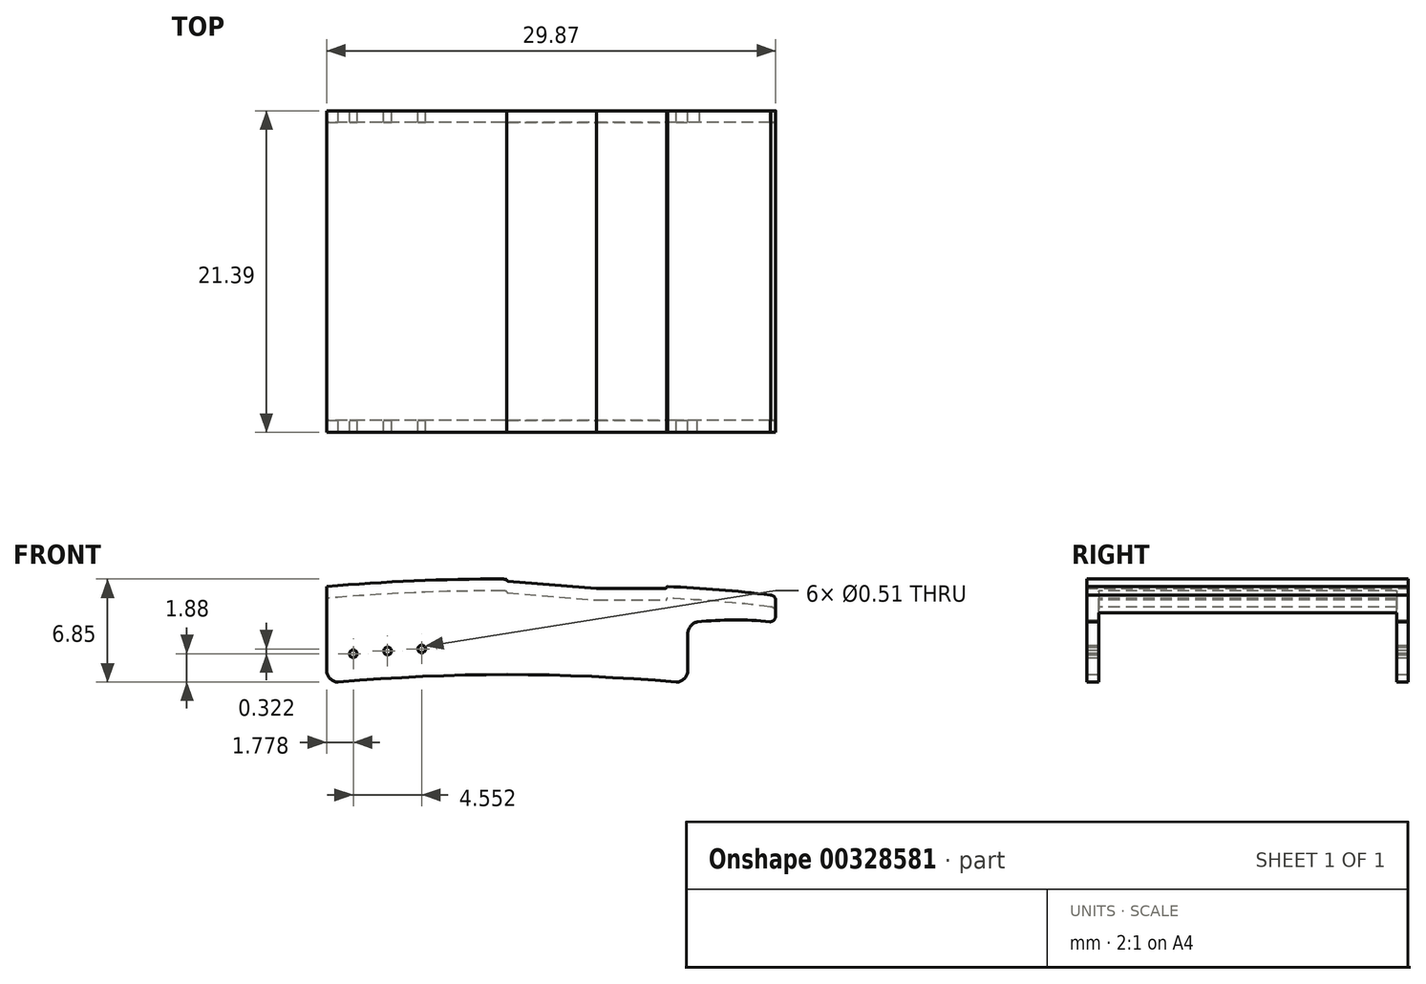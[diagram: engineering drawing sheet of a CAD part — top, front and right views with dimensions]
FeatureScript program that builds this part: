
annotation { "Feature Type Name" : "Feature", "Feature Type Description" : "" }
export const myFeature = defineFeature(function(context is Context, id is Id, definition is map)
    precondition{}
    {
        {
            var Q0;
            Q0=qCreatedBy(makeId("Front.planeOp"),FACE);
            var sketch = newSketch(context, id + "F0", { "sketchPlane" : qUnion([Q0])});
            skLineSegment(sketch, "E0", {"start": v(0, 0) * mm, "end": v(0, -5.56) * mm});
            skLineSegment(sketch, "E1", {"start": v(29.87, -1.96) * mm, "end": v(29.87, -0.94) * mm});
            skPoint(sketch, "E2.visualSharp", {"position": v(0, -6.35) * mm});
            skArc(sketch, "E2.filletArc", {"start": v(0, -5.56) * mm, "mid": v(0.23, -6.12) * mm, "end": v(0.79, -6.35) * mm});
            skLineSegment(sketch, "E3", {"start": v(24.03, -3.12) * mm, "end": v(24.03, -5.56) * mm});
            skPoint(sketch, "E4.orphan", {"position": v(29.87, -6.35) * mm});
            skPoint(sketch, "E5.visualSharp", {"position": v(24.03, -6.35) * mm});
            skArc(sketch, "E5.filletArc", {"start": v(23.24, -6.35) * mm, "mid": v(23.8, -6.12) * mm, "end": v(24.03, -5.56) * mm});
            skPoint(sketch, "E6.visualSharp", {"position": v(24.03, -2.34) * mm});
            skArc(sketch, "E6.filletArc", {"start": v(24.82, -2.34) * mm, "mid": v(24.26, -2.57) * mm, "end": v(24.03, -3.12) * mm});
            skPoint(sketch, "E7.visualSharp", {"position": v(29.87, -2.34) * mm});
            skArc(sketch, "E7.filletArc", {"start": v(29.49, -2.34) * mm, "mid": v(29.76, -2.23) * mm, "end": v(29.87, -1.96) * mm});
            skArc(sketch, "E8", {"start": v(23.24, -6.35) * mm, "mid": v(12.01, -5.85) * mm, "end": v(0.79, -6.35) * mm});
            skPoint(sketch, "E8.third.point", {"position": v(12.01, -259.85) * mm});
            skPoint(sketch, "E8.third.point.positionSnap0", {"position": v(12.01, -6.35) * mm});
            skPoint(sketch, "E9.endSnap0", {"position": v(12.01, -5.85) * mm});
            skArc(sketch, "E10", {"start": v(11.68, 0.5) * mm, "mid": v(5.84, 0.38) * mm, "end": v(0, 0) * mm});
            skPoint(sketch, "E11.third.point", {"position": v(17.97, 0) * mm});
            skPoint(sketch, "E12.visualSharp", {"position": v(11.84, 0.5) * mm});
            skArc(sketch, "E12.filletArc", {"start": v(11.95, 0.48) * mm, "mid": v(11.82, 0.5) * mm, "end": v(11.68, 0.5) * mm});
            skLineSegment(sketch, "E13", {"start": v(17.97, -0.1) * mm, "end": v(22.57, -0.1) * mm});
            skLineSegment(sketch, "E14", {"start": v(22.62, -0.06) * mm, "end": v(22.62, -0.05) * mm});
            skLineSegment(sketch, "E15", {"start": v(12, 0.43) * mm, "end": v(12, 0.42) * mm});
            skLineSegment(sketch, "E16", {"start": v(12.04, 0.37) * mm, "end": v(17.97, -0.1) * mm});
            skPoint(sketch, "E17.start.orphan", {"position": v(24.26, -2.57) * mm});
            skPoint(sketch, "E18.orphan", {"position": v(22.45, 0) * mm});
            skPoint(sketch, "E19.visualSharp", {"position": v(22.62, 0) * mm});
            skArc(sketch, "E19.filletArc", {"start": v(22.67, 0) * mm, "mid": v(22.63, -0.01) * mm, "end": v(22.62, -0.05) * mm});
            skPoint(sketch, "E20.visualSharp", {"position": v(22.62, -0.1) * mm});
            skArc(sketch, "E20.filletArc", {"start": v(22.57, -0.1) * mm, "mid": v(22.6, -0.1) * mm, "end": v(22.62, -0.06) * mm});
            skPoint(sketch, "E21.visualSharp", {"position": v(12, 0.37) * mm});
            skArc(sketch, "E21.filletArc", {"start": v(12, 0.42) * mm, "mid": v(12, 0.38) * mm, "end": v(12.04, 0.37) * mm});
            skPoint(sketch, "E22.visualSharp", {"position": v(12, 0.48) * mm});
            skArc(sketch, "E22.filletArc", {"start": v(12, 0.43) * mm, "mid": v(11.98, 0.47) * mm, "end": v(11.95, 0.48) * mm});
            skLineSegment(sketch, "E23", {"start": v(29.49, -2.34) * mm, "end": v(29.49, -1.96) * mm});
            skLineSegment(sketch, "E24", {"start": v(29.49, -0.56) * mm, "end": v(26.66, -0.33) * mm});
            skLineSegment(sketch, "E25", {"start": v(29.49, -0.56) * mm, "end": v(29.52, -0.56) * mm});
            skPoint(sketch, "E26.orphan", {"position": v(29.87, 0) * mm});
            skPoint(sketch, "E27.visualSharp", {"position": v(29.87, -0.6) * mm});
            skArc(sketch, "E27.filletArc", {"start": v(29.87, -0.94) * mm, "mid": v(29.77, -0.68) * mm, "end": v(29.52, -0.56) * mm});
            skArc(sketch, "E28", {"start": v(29.49, -2.34) * mm, "mid": v(27.07, -2.22) * mm, "end": v(24.65, -2.35) * mm});
            skPoint(sketch, "E28.third.point", {"position": v(27.15, -2.22) * mm});
            skPoint(sketch, "E28.third.point.positionSnap0", {"position": v(27.15, -2.34) * mm});
            skPoint(sketch, "E29.third.point", {"position": v(26.52, -0.25) * mm});
            skArc(sketch, "E30.trimOffspring", {"start": v(29.55, -0.57) * mm, "mid": v(26.12, -0.21) * mm, "end": v(22.67, 0) * mm});
            skCircle(sketch, "E31", {"center": v(1.78, -4.47) * mm, "radius": 0.25 * mm});
            skCircle(sketch, "E32", {"center": v(4.06, -4.29) * mm, "radius": 0.25 * mm});
            skCircle(sketch, "E33", {"center": v(6.33, -4.15) * mm, "radius": 0.25 * mm});
            skSolve(sketch);
        }
        {
            var Q0;
            Q0=makeQuery(id+"F0.imprint","IMPRINT",FACE,{"disambiguationData":[TD([[makeQuery(id+"F0.imprint","IMPRINT",EDGE,{"derivedFrom":sQuery(id+"F0.wireOp",EDGE,"E0")}),1.0]])]});
            extrude(context, id + "F1", {"entities" : qUnion([Q0]), "depth" : 0.79 * mm});
        }
        {
            var Q0;
            Q0=makeQuery(id+"F1.opExtrude","CAP_FACE",FACE,{"disambiguationData":[OSD([sQuery(id+"F0.wireOp",EDGE,"E0"),sQuery(id+"F0.wireOp",EDGE,"E1"),sQuery(id+"F0.wireOp",EDGE,"E2.filletArc"),sQuery(id+"F0.wireOp",EDGE,"E3"),sQuery(id+"F0.wireOp",EDGE,"E5.filletArc"),sQuery(id+"F0.wireOp",EDGE,"E6.filletArc"),sQuery(id+"F0.wireOp",EDGE,"E7.filletArc"),sQuery(id+"F0.wireOp",EDGE,"E8"),sQuery(id+"F0.wireOp",EDGE,"E10"),sQuery(id+"F0.wireOp",EDGE,"E12.filletArc"),sQuery(id+"F0.wireOp",EDGE,"E13"),sQuery(id+"F0.wireOp",EDGE,"E14"),sQuery(id+"F0.wireOp",EDGE,"E15"),sQuery(id+"F0.wireOp",EDGE,"E16"),sQuery(id+"F0.wireOp",EDGE,"E19.filletArc"),sQuery(id+"F0.wireOp",EDGE,"E20.filletArc"),sQuery(id+"F0.wireOp",EDGE,"E21.filletArc"),sQuery(id+"F0.wireOp",EDGE,"E22.filletArc"),sQuery(id+"F0.wireOp",EDGE,"E27.filletArc"),sQuery(id+"F0.wireOp",EDGE,"E28"),sQuery(id+"F0.wireOp",EDGE,"E30.trimOffspring")])],"isStart":false});
            cPlane(context, id + "F2", {"entities" : qUnion([Q0]), "cplaneType" : CPlaneType.OFFSET, "offset" : 19.8 * mm, "width" : 152.4 * mm, "height" : 152.4 * mm});
        }
        {
            var Q0;
            Q0=qCreatedBy(id+"F2.planeOp",FACE);
            var sketch = newSketch(context, id + "F3", { "sketchPlane" : qUnion([Q0])});
            skPoint(sketch, "E34.third.point", {"position": v(6.93, -255.26) * mm});
            skLineSegment(sketch, "E35", {"start": v(0, 0) * mm, "end": v(0, -5.56) * mm});
            skLineSegment(sketch, "E36", {"start": v(29.87, -1.96) * mm, "end": v(29.87, -0.94) * mm});
            skPoint(sketch, "E37.visualSharp", {"position": v(0, -6.35) * mm});
            skArc(sketch, "E37.filletArc", {"start": v(0, -5.56) * mm, "mid": v(0.23, -6.12) * mm, "end": v(0.79, -6.35) * mm});
            skLineSegment(sketch, "E38", {"start": v(24.03, -3.12) * mm, "end": v(24.03, -5.56) * mm});
            skPoint(sketch, "E39.visualSharp", {"position": v(24.03, -6.35) * mm});
            skArc(sketch, "E39.filletArc", {"start": v(23.24, -6.35) * mm, "mid": v(23.8, -6.12) * mm, "end": v(24.03, -5.56) * mm});
            skPoint(sketch, "E40.visualSharp", {"position": v(24.03, -2.34) * mm});
            skArc(sketch, "E40.filletArc", {"start": v(24.82, -2.34) * mm, "mid": v(24.26, -2.57) * mm, "end": v(24.03, -3.12) * mm});
            skPoint(sketch, "E41.visualSharp", {"position": v(29.87, -2.34) * mm});
            skArc(sketch, "E41.filletArc", {"start": v(29.49, -2.34) * mm, "mid": v(29.76, -2.23) * mm, "end": v(29.87, -1.96) * mm});
            skArc(sketch, "E42", {"start": v(23.24, -6.35) * mm, "mid": v(12.01, -5.85) * mm, "end": v(0.79, -6.35) * mm});
            skPoint(sketch, "E42.third.point", {"position": v(-6.13, -252.71) * mm});
            skPoint(sketch, "E42.third.point.positionSnap0", {"position": v(12.01, -6.35) * mm});
            skPoint(sketch, "E43.endSnap0", {"position": v(12.01, -5.85) * mm});
            skArc(sketch, "E44", {"start": v(11.68, 0.5) * mm, "mid": v(5.84, 0.38) * mm, "end": v(0, 0) * mm});
            skPoint(sketch, "E45.third.point", {"position": v(17.97, 0) * mm});
            skPoint(sketch, "E46.visualSharp", {"position": v(11.84, 0.5) * mm});
            skArc(sketch, "E46.filletArc", {"start": v(11.95, 0.48) * mm, "mid": v(11.82, 0.5) * mm, "end": v(11.68, 0.5) * mm});
            skLineSegment(sketch, "E47", {"start": v(17.97, -0.1) * mm, "end": v(22.57, -0.1) * mm});
            skLineSegment(sketch, "E48", {"start": v(22.62, -0.06) * mm, "end": v(22.62, -0.05) * mm});
            skLineSegment(sketch, "E49", {"start": v(12, 0.43) * mm, "end": v(12, 0.42) * mm});
            skLineSegment(sketch, "E50", {"start": v(12.04, 0.37) * mm, "end": v(17.97, -0.1) * mm});
            skPoint(sketch, "E51.start.orphan", {"position": v(24.26, -2.57) * mm});
            skPoint(sketch, "E52.orphan", {"position": v(22.45, 0) * mm});
            skPoint(sketch, "E53.visualSharp", {"position": v(22.62, 0) * mm});
            skArc(sketch, "E53.filletArc", {"start": v(22.67, 0) * mm, "mid": v(22.63, -0.01) * mm, "end": v(22.62, -0.05) * mm});
            skPoint(sketch, "E54.visualSharp", {"position": v(22.62, -0.1) * mm});
            skArc(sketch, "E54.filletArc", {"start": v(22.57, -0.1) * mm, "mid": v(22.6, -0.1) * mm, "end": v(22.62, -0.06) * mm});
            skPoint(sketch, "E55.visualSharp", {"position": v(12, 0.37) * mm});
            skArc(sketch, "E55.filletArc", {"start": v(12, 0.42) * mm, "mid": v(12, 0.38) * mm, "end": v(12.04, 0.37) * mm});
            skPoint(sketch, "E56.visualSharp", {"position": v(12, 0.48) * mm});
            skArc(sketch, "E56.filletArc", {"start": v(12, 0.43) * mm, "mid": v(11.98, 0.47) * mm, "end": v(11.95, 0.48) * mm});
            skLineSegment(sketch, "E57", {"start": v(29.49, -2.34) * mm, "end": v(29.49, -1.96) * mm});
            skLineSegment(sketch, "E58", {"start": v(29.49, -0.56) * mm, "end": v(26.66, -0.33) * mm});
            skLineSegment(sketch, "E59", {"start": v(29.49, -0.56) * mm, "end": v(29.52, -0.56) * mm});
            skPoint(sketch, "E60.orphan", {"position": v(29.87, 0) * mm});
            skPoint(sketch, "E61.visualSharp", {"position": v(29.87, -0.6) * mm});
            skArc(sketch, "E61.filletArc", {"start": v(29.87, -0.94) * mm, "mid": v(29.77, -0.68) * mm, "end": v(29.52, -0.56) * mm});
            skArc(sketch, "E62", {"start": v(29.49, -2.34) * mm, "mid": v(27.07, -2.22) * mm, "end": v(24.65, -2.35) * mm});
            skPoint(sketch, "E62.third.point", {"position": v(27.15, -2.22) * mm});
            skPoint(sketch, "E62.third.point.positionSnap0", {"position": v(27.15, -2.34) * mm});
            skPoint(sketch, "E63.third.point", {"position": v(26.52, -0.25) * mm});
            skArc(sketch, "E64.trimOffspring", {"start": v(29.55, -0.57) * mm, "mid": v(26.12, -0.21) * mm, "end": v(22.67, 0) * mm});
            skCircle(sketch, "E65", {"center": v(1.78, -4.47) * mm, "radius": 0.25 * mm});
            skCircle(sketch, "E66", {"center": v(4.06, -4.29) * mm, "radius": 0.25 * mm});
            skCircle(sketch, "E67", {"center": v(6.33, -4.15) * mm, "radius": 0.25 * mm});
            skSolve(sketch);
        }
        {
            var Q0;
            Q0 = qSketchRegion(id + "F3", true);
            extrude(context, id + "F4", {"entities" : qUnion([Q0]), "depth" : 0.79 * mm});
        }
        {
            var Q0;
            Q0=makeQuery(id+"F4.opExtrude","CAP_FACE",FACE,{"disambiguationData":[OSD([sQuery(id+"F3.wireOp",EDGE,"E35"),sQuery(id+"F3.wireOp",EDGE,"E36"),sQuery(id+"F3.wireOp",EDGE,"E37.filletArc"),sQuery(id+"F3.wireOp",EDGE,"E38"),sQuery(id+"F3.wireOp",EDGE,"E39.filletArc"),sQuery(id+"F3.wireOp",EDGE,"E40.filletArc"),sQuery(id+"F3.wireOp",EDGE,"E41.filletArc"),sQuery(id+"F3.wireOp",EDGE,"E42"),sQuery(id+"F3.wireOp",EDGE,"E44"),sQuery(id+"F3.wireOp",EDGE,"E46.filletArc"),sQuery(id+"F3.wireOp",EDGE,"E47"),sQuery(id+"F3.wireOp",EDGE,"E48"),sQuery(id+"F3.wireOp",EDGE,"E49"),sQuery(id+"F3.wireOp",EDGE,"E50"),sQuery(id+"F3.wireOp",EDGE,"E53.filletArc"),sQuery(id+"F3.wireOp",EDGE,"E54.filletArc"),sQuery(id+"F3.wireOp",EDGE,"E55.filletArc"),sQuery(id+"F3.wireOp",EDGE,"E56.filletArc"),sQuery(id+"F3.wireOp",EDGE,"E61.filletArc"),sQuery(id+"F3.wireOp",EDGE,"E62"),sQuery(id+"F3.wireOp",EDGE,"E64.trimOffspring"),sQuery(id+"F3.wireOp",EDGE,"E65"),sQuery(id+"F3.wireOp",EDGE,"E66"),sQuery(id+"F3.wireOp",EDGE,"E67")])],"isStart":false});
            var sketch = newSketch(context, id + "F5", { "sketchPlane" : qUnion([Q0])});
            skLineSegment(sketch, "E68", {"start": v(29.87, -1.96) * mm, "end": v(29.87, -0.94) * mm});
            skLineSegment(sketch, "E69", {"start": v(24.03, -3.12) * mm, "end": v(24.03, -5.56) * mm});
            skPoint(sketch, "E70.orphan", {"position": v(29.87, -6.35) * mm});
            skPoint(sketch, "E71.visualSharp", {"position": v(24.03, -6.35) * mm});
            skArc(sketch, "E71.filletArc", {"start": v(23.24, -6.35) * mm, "mid": v(23.8, -6.12) * mm, "end": v(24.03, -5.56) * mm});
            skPoint(sketch, "E72.visualSharp", {"position": v(24.03, -2.34) * mm});
            skArc(sketch, "E72.filletArc", {"start": v(24.82, -2.34) * mm, "mid": v(24.26, -2.57) * mm, "end": v(24.03, -3.12) * mm});
            skArc(sketch, "E73.filletArc", {"start": v(29.49, -2.34) * mm, "mid": v(29.76, -2.23) * mm, "end": v(29.87, -1.96) * mm});
            skPoint(sketch, "E74.third.point", {"position": v(-12.98, -247.84) * mm});
            skPoint(sketch, "E74.third.point.positionSnap0", {"position": v(12.01, -6.35) * mm});
            skPoint(sketch, "E75.endSnap0", {"position": v(12.01, -5.85) * mm});
            skArc(sketch, "E76", {"start": v(11.68, 0.5) * mm, "mid": v(5.84, 0.38) * mm, "end": v(0, 0) * mm});
            skPoint(sketch, "E77.third.point", {"position": v(17.97, 0) * mm});
            skPoint(sketch, "E78.visualSharp", {"position": v(11.84, 0.5) * mm});
            skArc(sketch, "E78.filletArc", {"start": v(11.95, 0.48) * mm, "mid": v(11.82, 0.5) * mm, "end": v(11.68, 0.5) * mm});
            skLineSegment(sketch, "E79", {"start": v(17.97, -0.1) * mm, "end": v(22.57, -0.1) * mm});
            skLineSegment(sketch, "E80", {"start": v(22.62, -0.06) * mm, "end": v(22.62, -0.05) * mm});
            skLineSegment(sketch, "E81", {"start": v(12, 0.43) * mm, "end": v(12, 0.42) * mm});
            skLineSegment(sketch, "E82", {"start": v(12.04, 0.37) * mm, "end": v(17.97, -0.1) * mm});
            skPoint(sketch, "E83.start.orphan", {"position": v(24.26, -2.57) * mm});
            skPoint(sketch, "E84.orphan", {"position": v(22.45, 0) * mm});
            skPoint(sketch, "E85.visualSharp", {"position": v(22.62, 0) * mm});
            skArc(sketch, "E85.filletArc", {"start": v(22.67, 0) * mm, "mid": v(22.63, -0.01) * mm, "end": v(22.62, -0.05) * mm});
            skPoint(sketch, "E86.visualSharp", {"position": v(22.62, -0.1) * mm});
            skArc(sketch, "E86.filletArc", {"start": v(22.57, -0.1) * mm, "mid": v(22.6, -0.1) * mm, "end": v(22.62, -0.06) * mm});
            skPoint(sketch, "E87.visualSharp", {"position": v(12, 0.37) * mm});
            skArc(sketch, "E87.filletArc", {"start": v(12, 0.42) * mm, "mid": v(12, 0.38) * mm, "end": v(12.04, 0.37) * mm});
            skPoint(sketch, "E88.visualSharp", {"position": v(12, 0.48) * mm});
            skArc(sketch, "E88.filletArc", {"start": v(12, 0.43) * mm, "mid": v(11.98, 0.47) * mm, "end": v(11.95, 0.48) * mm});
            skLineSegment(sketch, "E89", {"start": v(29.49, -2.34) * mm, "end": v(29.49, -1.96) * mm});
            skLineSegment(sketch, "E90", {"start": v(29.49, -0.56) * mm, "end": v(26.66, -0.33) * mm});
            skLineSegment(sketch, "E91", {"start": v(29.49, -0.56) * mm, "end": v(29.52, -0.56) * mm});
            skPoint(sketch, "E92.orphan", {"position": v(29.87, 0) * mm});
            skPoint(sketch, "E93.visualSharp", {"position": v(29.87, -0.6) * mm});
            skArc(sketch, "E93.filletArc", {"start": v(29.87, -0.94) * mm, "mid": v(29.77, -0.68) * mm, "end": v(29.52, -0.56) * mm});
            skArc(sketch, "E94", {"start": v(29.49, -2.34) * mm, "mid": v(27.07, -2.22) * mm, "end": v(24.65, -2.35) * mm});
            skPoint(sketch, "E94.third.point", {"position": v(27.15, -2.22) * mm});
            skPoint(sketch, "E94.third.point.positionSnap0", {"position": v(27.15, -2.34) * mm});
            skPoint(sketch, "E95.third.point", {"position": v(26.52, -0.25) * mm});
            skArc(sketch, "E96.trimOffspring", {"start": v(29.55, -0.57) * mm, "mid": v(26.12, -0.21) * mm, "end": v(22.67, 0) * mm});
            skLineSegment(sketch, "E97", {"start": v(0, 0) * mm, "end": v(0, -0.79) * mm});
            skArc(sketch, "E98", {"start": v(11.68, -0.3) * mm, "mid": v(5.84, -0.4) * mm, "end": v(0, -0.79) * mm});
            skPoint(sketch, "E99.third.point", {"position": v(17.97, -0.79) * mm});
            skPoint(sketch, "E100.visualSharp", {"position": v(11.84, -0.3) * mm});
            skArc(sketch, "E100.filletArc", {"start": v(11.95, -0.3) * mm, "mid": v(11.82, -0.3) * mm, "end": v(11.68, -0.3) * mm});
            skLineSegment(sketch, "E101", {"start": v(17.97, -0.9) * mm, "end": v(22.57, -0.9) * mm});
            skLineSegment(sketch, "E102", {"start": v(22.62, -0.85) * mm, "end": v(22.62, -0.84) * mm});
            skLineSegment(sketch, "E103", {"start": v(12, -0.36) * mm, "end": v(12, -0.37) * mm});
            skLineSegment(sketch, "E104", {"start": v(12.04, -0.42) * mm, "end": v(17.97, -0.9) * mm});
            skPoint(sketch, "E105.orphan", {"position": v(22.45, -0.79) * mm});
            skPoint(sketch, "E106.visualSharp", {"position": v(22.62, -0.79) * mm});
            skArc(sketch, "E106.filletArc", {"start": v(22.67, -0.79) * mm, "mid": v(22.63, -0.8) * mm, "end": v(22.62, -0.84) * mm});
            skPoint(sketch, "E107.visualSharp", {"position": v(22.62, -0.9) * mm});
            skArc(sketch, "E107.filletArc", {"start": v(22.57, -0.9) * mm, "mid": v(22.6, -0.88) * mm, "end": v(22.62, -0.85) * mm});
            skPoint(sketch, "E108.visualSharp", {"position": v(12, -0.42) * mm});
            skArc(sketch, "E108.filletArc", {"start": v(12, -0.37) * mm, "mid": v(12, -0.4) * mm, "end": v(12.04, -0.42) * mm});
            skPoint(sketch, "E109.visualSharp", {"position": v(12, -0.31) * mm});
            skArc(sketch, "E109.filletArc", {"start": v(12, -0.36) * mm, "mid": v(11.98, -0.32) * mm, "end": v(11.95, -0.3) * mm});
            skLineSegment(sketch, "E110", {"start": v(29.49, -1.35) * mm, "end": v(26.66, -1.11) * mm});
            skLineSegment(sketch, "E111", {"start": v(29.49, -1.35) * mm, "end": v(29.52, -1.35) * mm});
            skPoint(sketch, "E112.orphan", {"position": v(29.87, -0.79) * mm});
            skPoint(sketch, "E113.visualSharp", {"position": v(29.87, -1.38) * mm});
            skArc(sketch, "E113.filletArc", {"start": v(29.87, -1.73) * mm, "mid": v(29.77, -1.47) * mm, "end": v(29.52, -1.35) * mm});
            skPoint(sketch, "E114.third.point", {"position": v(26.52, -1.03) * mm});
            skArc(sketch, "E115.trimOffspring", {"start": v(29.55, -1.35) * mm, "mid": v(26.12, -1) * mm, "end": v(22.67, -0.79) * mm});
            skSolve(sketch);
        }
        {
            var Q0;
            Q0=makeQuery(id+"F5.imprint","IMPRINT",FACE,{"disambiguationData":[TD([[makeQuery(id+"F5.imprint","IMPRINT",EDGE,{"derivedFrom":sQuery(id+"F5.wireOp",EDGE,"E76")}),1.0]])]});
            extrude(context, id + "F6", {"entities" : qUnion([Q0]), "operationType" : NewBodyOperationType.ADD, "oppositeDirection" : true, "depth" : 20.83 * mm});
        }
    });
